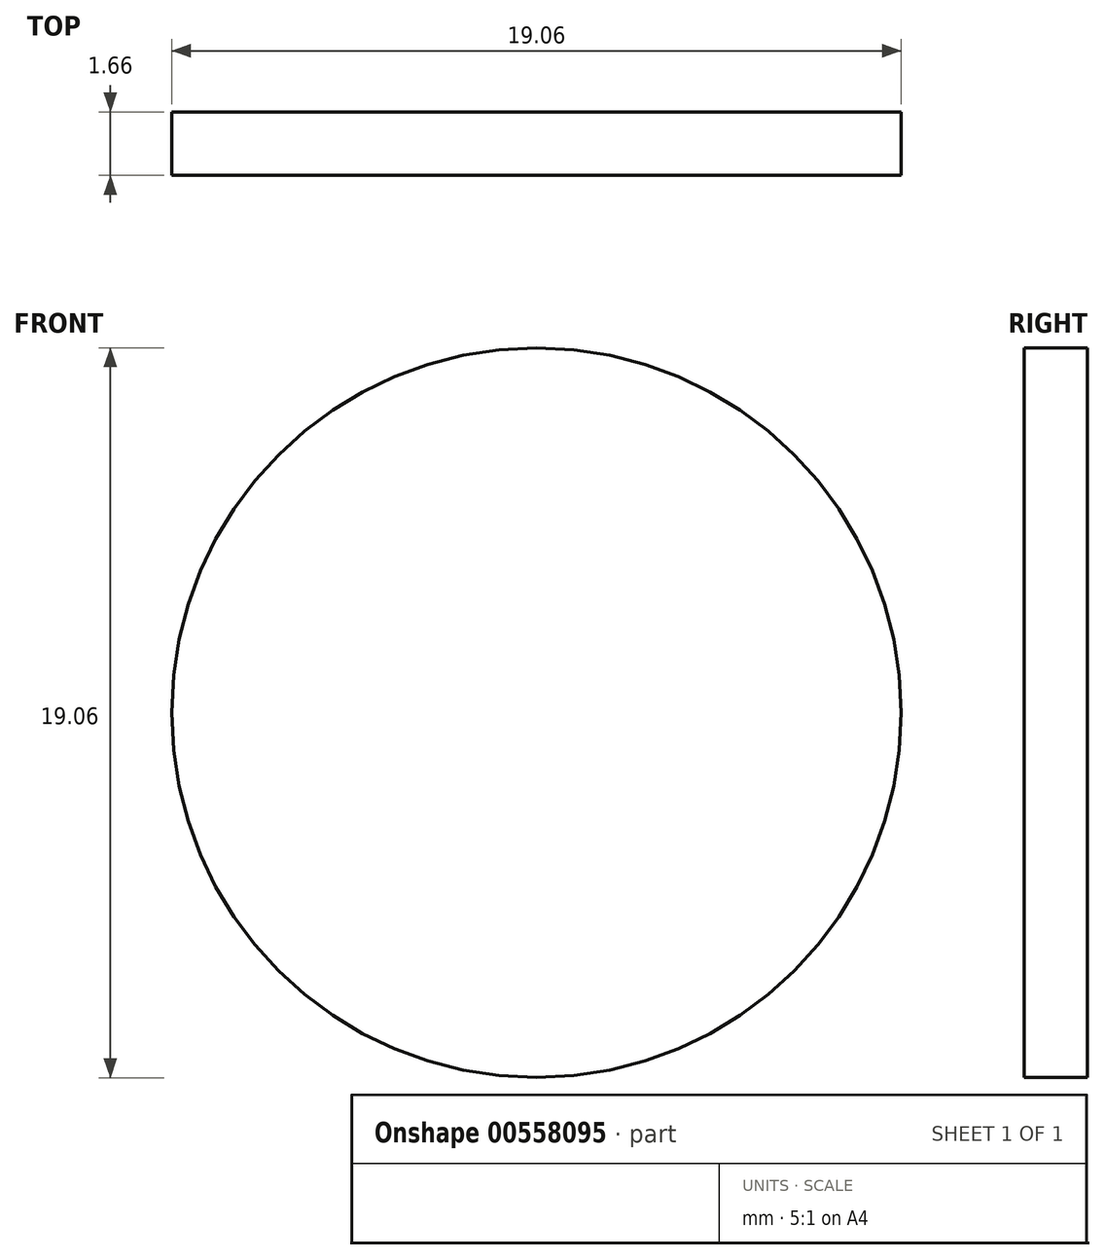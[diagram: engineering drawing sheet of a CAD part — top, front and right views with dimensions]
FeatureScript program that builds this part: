
annotation { "Feature Type Name" : "Feature", "Feature Type Description" : "" }
export const myFeature = defineFeature(function(context is Context, id is Id, definition is map)
    precondition{}
    {
        {
            var Q0;
            Q0=qCreatedBy(makeId("Front.planeOp"),FACE);
            var sketch = newSketch(context, id + "F0", { "sketchPlane" : qUnion([Q0])});
            skCircle(sketch, "E0", {"center": v(0, 0) * mm, "radius": 9.53 * mm});
            skSolve(sketch);
        }
        {
            var Q0;
            Q0 = qSketchRegion(id + "F0", true);
            extrude(context, id + "F1", {"entities" : qUnion([Q0]), "endBound" : BoundingType.SYMMETRIC, "depth" : 1.65 * mm, "offsetDistance" : 25.4 * mm});
        }
    });
